# Revit family: NLRS_57_AIR_UN_exhaust-deflektor-hood-vdk-with-options_LT_velu
name_source: partatom
category: Air Terminals
units: mm (PartAtom-declared; Revit-internal decimal feet)

## family parameters
Always vertical = No
Cut with Voids When Loaded = No
Part Type = Normal
Room Calculation Point = No
Round Connector Dimension = Use Diameter
Shared = No
Work Plane-Based = No

## types (3) — shared parameters
Assembly Code = 57.00
Description = Velu uitblaas deflectorkap, type VDK
FireRating = 00
IfcDescription = Velu uitblaas deflectorkap, type VDK
IfcExportAs = IfcAirterminal
IfcExportType = Diffuser
IsExternal = Yes
LT = VDK_Data
LoadBearing = No
Manufacturer = Velu Ventilatietechniek BV
Model = VDK
NLRS_C_content_datum_uitgifte = 27-05-2022
NLRS_C_content_provider = Velu Ventliatietechniek BV
NLRS_C_content_versie = 3.19.00
NLRS_C_description = Velu uitblaas deflectorkap, type VDK
NLRS_C_niveau ontwikkeling = LOD400
SACS_Angle1 = 26.57°
URL = https://velu.nl

## per-type parameters (varying)
| type | SACS_Show_Part_1 | SACS_Show_Part_2 |
| Deflectorkap VDK | No | No |
| Deflectorkap VDK + Stormkraag VSK | Yes | No |
| Deflectorkap VDK + VSK + Plakplaat VPL | Yes | Yes |

## geometry (parser evidence)
native form markers: Sweep x14
no freeform markers — native parametric forms only
